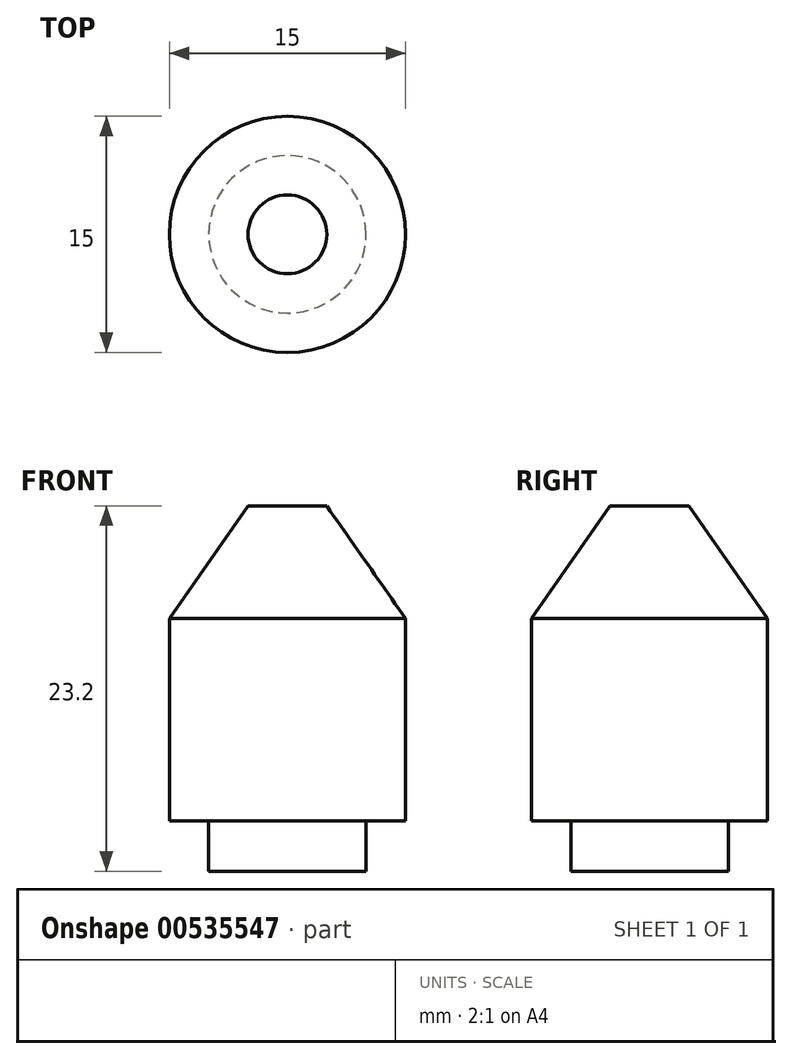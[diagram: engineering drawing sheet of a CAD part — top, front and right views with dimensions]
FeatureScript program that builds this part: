
annotation { "Feature Type Name" : "Feature", "Feature Type Description" : "" }
export const myFeature = defineFeature(function(context is Context, id is Id, definition is map)
    precondition{}
    {
        {
            var Q0;
            Q0=qCreatedBy(makeId("Top.planeOp"),FACE);
            var sketch = newSketch(context, id + "F0", { "sketchPlane" : qUnion([Q0])});
            skCircle(sketch, "E0", {"center": v(0, 0) * mm, "radius": 7.5 * mm});
            skSolve(sketch);
        }
        {
            var Q0;
            Q0 = qSketchRegion(id + "F0", true);
            extrude(context, id + "F1", {"entities" : qUnion([Q0]), "depth" : 20 * mm, "offsetDistance" : 25 * mm});
        }
        {
            var Q0;
            Q0=makeQuery(id+"F1.opExtrude","CAP_EDGE",EDGE,{"disambiguationData":[OSD([sQuery(id+"F0.wireOp",EDGE,"E0")])],"isStart":false});
            chamfer(context, id + "F2", {"entities" : qUnion([Q0]), "chamferType" : ChamferType.OFFSET_ANGLE, "width" : 5 * mm, "oppositeDirection" : false, "angle" : 55 * degree, "tangentPropagation" : true});
        }
        {
            var Q0;
            Q0=qCreatedBy(makeId("Top.planeOp"),FACE);
            var sketch = newSketch(context, id + "F3", { "sketchPlane" : qUnion([Q0])});
            skCircle(sketch, "E1", {"center": v(0, 0) * mm, "radius": 5 * mm});
            skSolve(sketch);
        }
        {
            var Q0;
            Q0 = qSketchRegion(id + "F3", true);
            extrude(context, id + "F4", {"entities" : qUnion([Q0]), "operationType" : NewBodyOperationType.ADD, "oppositeDirection" : true, "depth" : 3.2 * mm, "offsetDistance" : 25 * mm});
        }
    });
